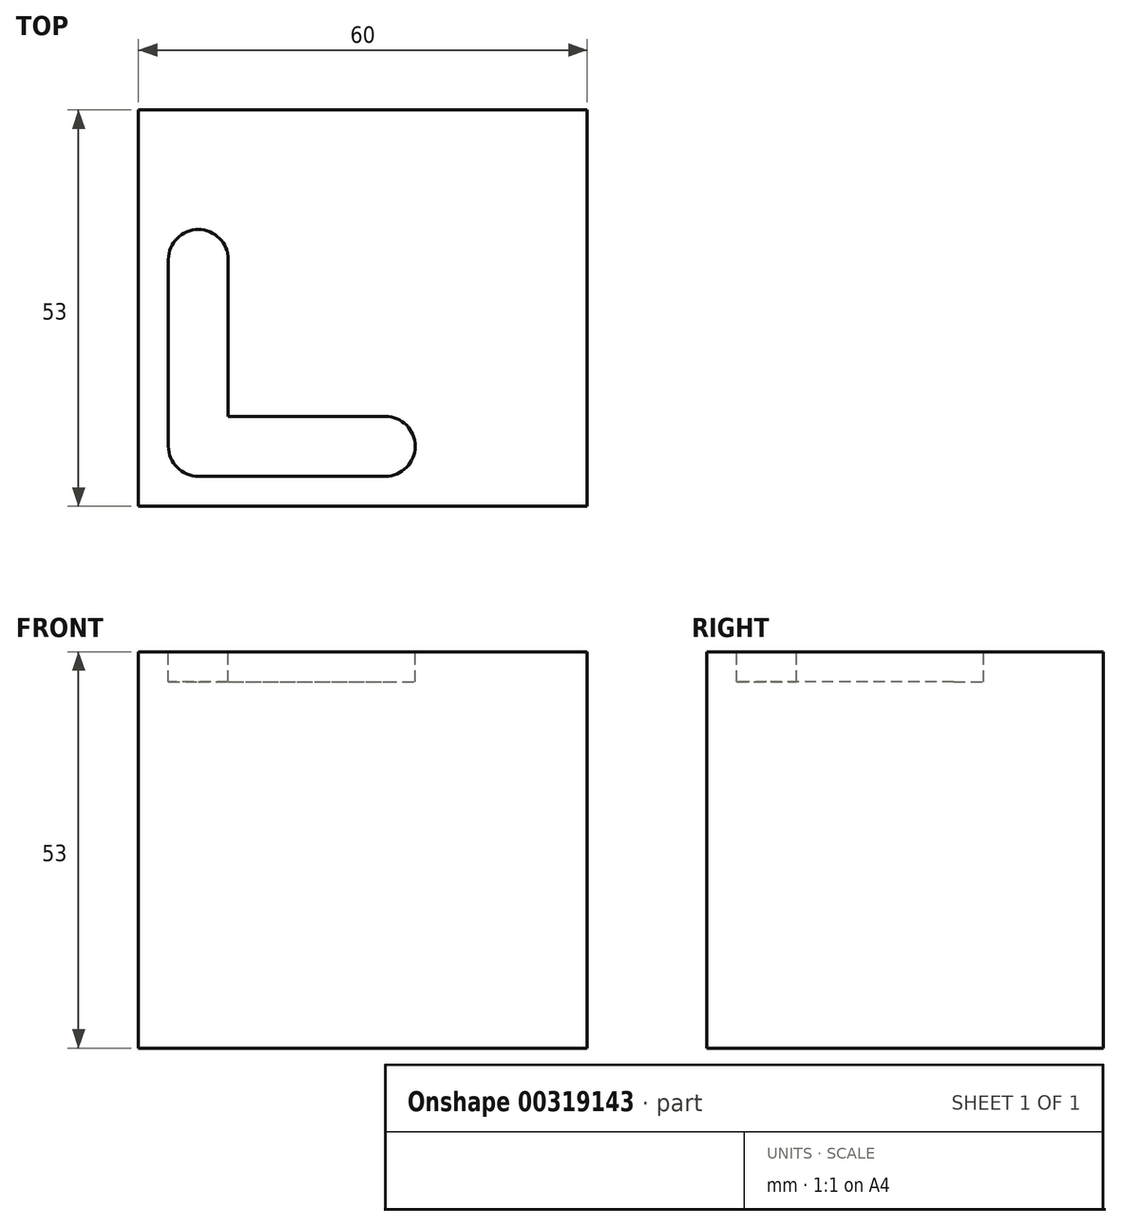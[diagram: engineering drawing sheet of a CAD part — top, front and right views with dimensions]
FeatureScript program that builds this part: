
annotation { "Feature Type Name" : "Feature", "Feature Type Description" : "" }
export const myFeature = defineFeature(function(context is Context, id is Id, definition is map)
    precondition{}
    {
        {
            var Q0;
            Q0=qCreatedBy(makeId("Right.planeOp"),FACE);
            var sketch = newSketch(context, id + "F0", { "sketchPlane" : qUnion([Q0])});
            skLineSegment(sketch, "E0.bottom", {"start": v(0, 0) * mm, "end": v(53, 0) * mm});
            skLineSegment(sketch, "E0.top", {"start": v(0, 53) * mm, "end": v(53, 53) * mm});
            skLineSegment(sketch, "E0.left", {"start": v(0, 0) * mm, "end": v(0, 53) * mm});
            skLineSegment(sketch, "E0.right", {"start": v(53, 0) * mm, "end": v(53, 53) * mm});
            skSolve(sketch);
        }
        {
            var Q0;
            Q0=makeQuery(id+"F0.imprint","IMPRINT",FACE,{"disambiguationData":[TD([[makeQuery(id+"F0.imprint","IMPRINT",EDGE,{"derivedFrom":sQuery(id+"F0.wireOp",EDGE,"E0.bottom")}),1.0]])]});
            extrude(context, id + "F1", {"entities" : qUnion([Q0]), "depth" : 60 * mm});
        }
        {
            var Q0;
            Q0=makeQuery(id+"F1.opExtrude","SWEPT_FACE",FACE,{"disambiguationData":[OSD([sQuery(id+"F0.wireOp",EDGE,"E0.top")])]});
            var sketch = newSketch(context, id + "F2", { "sketchPlane" : qUnion([Q0])});
            skLineSegment(sketch, "E1", {"start": v(8, 33) * mm, "end": v(8, 8) * mm, "construction": true});
            skLineSegment(sketch, "E2", {"start": v(8, 8) * mm, "end": v(33, 8) * mm, "construction": true});
            skArc(sketch, "E3.0.startCap", {"start": v(4, 33) * mm, "mid": v(8, 37) * mm, "end": v(12, 33) * mm});
            skArc(sketch, "E3.0.endCap", {"start": v(12, 8) * mm, "mid": v(8, 4) * mm, "end": v(4, 8) * mm});
            skLineSegment(sketch, "E3.0.left", {"start": v(12, 33) * mm, "end": v(12, 12) * mm});
            skLineSegment(sketch, "E3.0.right", {"start": v(4, 33) * mm, "end": v(4, 8) * mm});
            skArc(sketch, "E3.1.startCap", {"start": v(8, 4) * mm, "mid": v(4, 8) * mm, "end": v(8, 12) * mm});
            skArc(sketch, "E3.1.endCap", {"start": v(33, 12) * mm, "mid": v(37, 8) * mm, "end": v(33, 4) * mm});
            skLineSegment(sketch, "E3.1.left", {"start": v(12, 12) * mm, "end": v(33, 12) * mm});
            skLineSegment(sketch, "E3.1.right", {"start": v(8, 4) * mm, "end": v(33, 4) * mm});
            skSolve(sketch);
        }
        {
            var Q0;
            Q0 = qSketchRegion(id + "F2", true);
            extrude(context, id + "F3", {"entities" : qUnion([Q0]), "operationType" : NewBodyOperationType.REMOVE, "oppositeDirection" : true, "depth" : 4 * mm});
        }
    });
